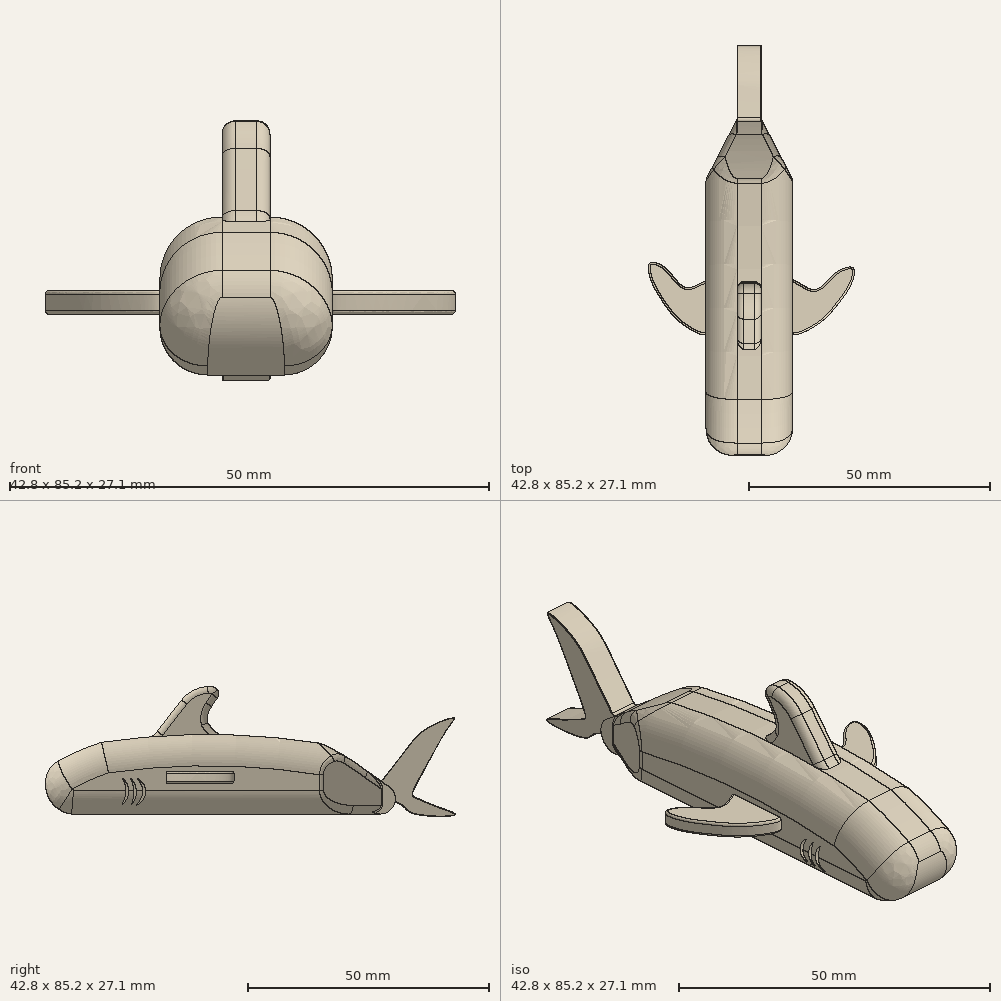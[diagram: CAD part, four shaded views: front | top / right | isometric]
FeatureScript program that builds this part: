
annotation { "Feature Type Name" : "Feature", "Feature Type Description" : "" }
export const myFeature = defineFeature(function(context is Context, id is Id, definition is map)
    precondition{}
    {
        {
            var Q0;
            Q0=qCreatedBy(makeId("Right.planeOp"),FACE);
            cPlane(context, id + "F0", {"entities" : qUnion([Q0]), "cplaneType" : CPlaneType.OFFSET, "offset" : 6.5 * mm, "width" : 150 * mm, "height" : 150 * mm});
        }
        {
            var Q0;
            Q0=qCreatedBy(makeId("Top.planeOp"),FACE);
            cPlane(context, id + "F1", {"entities" : qUnion([Q0]), "cplaneType" : CPlaneType.OFFSET, "offset" : 4.2 * mm, "oppositeDirection" : true, "width" : 150 * mm, "height" : 150 * mm});
        }
        {
            var Q0;
            Q0=qCreatedBy(makeId("Right.planeOp"),FACE);
            cPlane(context, id + "F2", {"entities" : qUnion([Q0]), "cplaneType" : CPlaneType.OFFSET, "offset" : 18 * mm, "width" : 150 * mm, "height" : 150 * mm});
        }
        {
            var Q0;
            Q0=qCreatedBy(makeId("Right.planeOp"),FACE);
            var sketch = newSketch(context, id + "F3", { "sketchPlane" : qUnion([Q0])});
            skLineSegment(sketch, "E0", {"start": v(-39.86, -13.02) * mm, "end": v(24.33, -13.02) * mm});
            skArc(sketch, "E1", {"start": v(-43.75, -2.7) * mm, "mid": v(-44.9, -9.03) * mm, "end": v(-39.86, -13.02) * mm});
            skArc(sketch, "E2", {"start": v(-33.67, 1.88) * mm, "mid": v(-38.84, -0.12) * mm, "end": v(-43.75, -2.7) * mm});
            skArc(sketch, "E3", {"start": v(11.79, 1.7) * mm, "mid": v(-10.93, 3.51) * mm, "end": v(-33.67, 1.88) * mm});
            skArc(sketch, "E4", {"start": v(21.4, -4.04) * mm, "mid": v(16.77, -0.87) * mm, "end": v(11.79, 1.7) * mm});
            skArc(sketch, "E5", {"start": v(25.54, -7) * mm, "mid": v(23.5, -5.48) * mm, "end": v(21.4, -4.04) * mm});
            skArc(sketch, "E6", {"start": v(24.33, -13.02) * mm, "mid": v(27.4, -10.51) * mm, "end": v(25.54, -7) * mm});
            skSolve(sketch);
        }
        {
            var Q0;
            {var subQ0=sQuery(id+"F3.wireOp",EDGE,"4997cbf1-64fe-4e0f-b577-89496dce1422");var subQ1=sQuery(id+"F3.wireOp",EDGE,"E0");var subQ2=makeQuery(id+"F3.imprint","INTERSECT",VERTEX,{"derivedFrom":[subQ1,subQ0]});Q0=makeQuery(id+"F3.imprint","IMPRINT",FACE,{"disambiguationData":[TD([[makeQuery(id+"F3.imprint","IMPRINT",EDGE,{"disambiguationData":[TD([[subQ2,-1.0]])],"derivedFrom":subQ1}),1.0]])]});}
            extrude(context, id + "F4", {"entities" : qUnion([Q0]), "depth" : 18 * mm, "offsetDistance" : 25 * mm});
        }
        {
            var Q0;
            Q0=makeQuery(id+"F4.opExtrude","CAP_EDGE",EDGE,{"disambiguationData":[OSD([sQuery(id+"F3.wireOp",EDGE,"E3")])],"isStart":false});
            var Q1;
            Q1=makeQuery(id+"F4.opExtrude","CAP_EDGE",EDGE,{"disambiguationData":[OSD([sQuery(id+"F3.wireOp",EDGE,"E3")])],"isStart":true});
            var Q2;
            Q2=makeQuery(id+"F4.opExtrude","CAP_EDGE",EDGE,{"disambiguationData":[OSD([sQuery(id+"F3.wireOp",EDGE,"E2")])],"isStart":true});
            var Q3;
            Q3=makeQuery(id+"F4.opExtrude","CAP_EDGE",EDGE,{"disambiguationData":[OSD([sQuery(id+"F3.wireOp",EDGE,"E2")])],"isStart":false});
            fillet(context, id + "F5", {"entities" : qUnion([Q0, Q1, Q2, Q3]), "radius" : 6.5 * mm, "allowEdgeOverflow" : false});
        }
        {
            var Q0;
            Q0=qCreatedBy(id+"F0.planeOp",FACE);
            var sketch = newSketch(context, id + "F6", { "sketchPlane" : qUnion([Q0])});
            skArc(sketch, "E7", {"start": v(-24.68, 2.43) * mm, "mid": v(-23.19, 3.05) * mm, "end": v(-22.01, 4.15) * mm});
            skArc(sketch, "E8", {"start": v(-16.96, 10.65) * mm, "mid": v(-19.5, 7.41) * mm, "end": v(-22.01, 4.15) * mm});
            skArc(sketch, "E9", {"start": v(-11.69, 13.48) * mm, "mid": v(-14.61, 12.6) * mm, "end": v(-16.96, 10.65) * mm});
            skArc(sketch, "E10", {"start": v(-9.52, 12.75) * mm, "mid": v(-10.5, 13.41) * mm, "end": v(-11.69, 13.48) * mm});
            skArc(sketch, "E11", {"start": v(-9.52, 11.03) * mm, "mid": v(-9.25, 11.89) * mm, "end": v(-9.52, 12.75) * mm});
            skArc(sketch, "E12", {"start": v(-9.52, 11.03) * mm, "mid": v(-10.16, 10.16) * mm, "end": v(-10.73, 9.25) * mm});
            skArc(sketch, "E13", {"start": v(-10.73, 9.25) * mm, "mid": v(-11.52, 7.68) * mm, "end": v(-11.54, 5.92) * mm});
            skArc(sketch, "E14", {"start": v(-11.54, 5.92) * mm, "mid": v(-9.81, 3.95) * mm, "end": v(-7.55, 2.65) * mm});
            skArc(sketch, "E15", {"start": v(-24.68, 2.43) * mm, "mid": v(-16.1, 1.6) * mm, "end": v(-7.55, 2.65) * mm});
            skSolve(sketch);
        }
        {
            var Q0;
            Q0 = qSketchRegion(id + "F6", true);
            extrude(context, id + "F7", {"entities" : qUnion([Q0]), "depth" : 5 * mm, "offsetDistance" : 25 * mm});
        }
        {
            var Q0;
            Q0=makeQuery(id+"F7.opExtrude","CAP_EDGE",EDGE,{"disambiguationData":[OSD([sQuery(id+"F6.wireOp",EDGE,"E11")])],"isStart":false});
            var Q1;
            Q1=makeQuery(id+"F7.opExtrude","CAP_EDGE",EDGE,{"disambiguationData":[OSD([sQuery(id+"F6.wireOp",EDGE,"E12")])],"isStart":false});
            var Q2;
            Q2=makeQuery(id+"F7.opExtrude","CAP_EDGE",EDGE,{"disambiguationData":[OSD([sQuery(id+"F6.wireOp",EDGE,"E13")])],"isStart":false});
            var Q3;
            Q3=makeQuery(id+"F7.opExtrude","CAP_EDGE",EDGE,{"disambiguationData":[OSD([sQuery(id+"F6.wireOp",EDGE,"E14")])],"isStart":false});
            var Q4;
            Q4=makeQuery(id+"F7.opExtrude","CAP_EDGE",EDGE,{"disambiguationData":[OSD([sQuery(id+"F6.wireOp",EDGE,"E10")])],"isStart":false});
            var Q5;
            Q5=makeQuery(id+"F7.opExtrude","CAP_EDGE",EDGE,{"disambiguationData":[OSD([sQuery(id+"F6.wireOp",EDGE,"E10")])],"isStart":true});
            var Q6;
            Q6=makeQuery(id+"F7.opExtrude","CAP_EDGE",EDGE,{"disambiguationData":[OSD([sQuery(id+"F6.wireOp",EDGE,"E11")])],"isStart":true});
            var Q7;
            Q7=makeQuery(id+"F7.opExtrude","CAP_EDGE",EDGE,{"disambiguationData":[OSD([sQuery(id+"F6.wireOp",EDGE,"E12")])],"isStart":true});
            var Q8;
            Q8=makeQuery(id+"F7.opExtrude","CAP_EDGE",EDGE,{"disambiguationData":[OSD([sQuery(id+"F6.wireOp",EDGE,"E13")])],"isStart":true});
            var Q9;
            Q9=makeQuery(id+"F7.opExtrude","CAP_EDGE",EDGE,{"disambiguationData":[OSD([sQuery(id+"F6.wireOp",EDGE,"E14")])],"isStart":true});
            var Q10;
            Q10=makeQuery(id+"F7.opExtrude","CAP_EDGE",EDGE,{"disambiguationData":[OSD([sQuery(id+"F6.wireOp",EDGE,"E9")])],"isStart":false});
            var Q11;
            Q11=makeQuery(id+"F7.opExtrude","CAP_EDGE",EDGE,{"disambiguationData":[OSD([sQuery(id+"F6.wireOp",EDGE,"E8")])],"isStart":false});
            var Q12;
            Q12=makeQuery(id+"F7.opExtrude","CAP_EDGE",EDGE,{"disambiguationData":[OSD([sQuery(id+"F6.wireOp",EDGE,"E7")])],"isStart":false});
            var Q13;
            Q13=makeQuery(id+"F7.opExtrude","CAP_EDGE",EDGE,{"disambiguationData":[OSD([sQuery(id+"F6.wireOp",EDGE,"E7")])],"isStart":true});
            var Q14;
            Q14=makeQuery(id+"F7.opExtrude","CAP_EDGE",EDGE,{"disambiguationData":[OSD([sQuery(id+"F6.wireOp",EDGE,"E8")])],"isStart":true});
            var Q15;
            Q15=makeQuery(id+"F7.opExtrude","CAP_EDGE",EDGE,{"disambiguationData":[OSD([sQuery(id+"F6.wireOp",EDGE,"E9")])],"isStart":true});
            fillet(context, id + "F8", {"entities" : qUnion([Q0, Q1, Q2, Q3, Q4, Q5, Q6, Q7, Q8, Q9, Q10, Q11, Q12, Q13, Q14, Q15]), "radius" : 1.4 * mm, "tangentPropagation" : true, "allowEdgeOverflow" : false});
        }
        {
            var Q0;
            Q0=makeQuery(id+"F5.opFillet","BLEND_EDGE",EDGE,{"blendedFrom":[makeQuery(id+"F4.opExtrude","CAP_EDGE",EDGE,{"disambiguationData":[OSD([sQuery(id+"F3.wireOp",EDGE,"E3")])],"isStart":true}),makeQuery(id+"F4.opExtrude","SWEPT_FACE",FACE,{"disambiguationData":[OSD([sQuery(id+"F3.wireOp",EDGE,"E5")])]})],"blendedInto":[makeQuery(id+"F4.opExtrude","SWEPT_FACE",FACE,{"disambiguationData":[OSD([sQuery(id+"F3.wireOp",EDGE,"E5")])]})]});
            var Q1;
            Q1=makeQuery(id+"F5.opFillet","BLEND_EDGE",EDGE,{"blendedFrom":[makeQuery(id+"F4.opExtrude","CAP_EDGE",EDGE,{"disambiguationData":[OSD([sQuery(id+"F3.wireOp",EDGE,"E3")])],"isStart":true}),makeQuery(id+"F4.opExtrude","SWEPT_FACE",FACE,{"disambiguationData":[OSD([sQuery(id+"F3.wireOp",EDGE,"E4")])]})],"blendedInto":[makeQuery(id+"F4.opExtrude","SWEPT_FACE",FACE,{"disambiguationData":[OSD([sQuery(id+"F3.wireOp",EDGE,"E4")])]})]});
            var Q2;
            Q2=makeQuery(id+"F5.opFillet","BLEND_EDGE",EDGE,{"blendedFrom":[makeQuery(id+"F4.opExtrude","CAP_EDGE",EDGE,{"disambiguationData":[OSD([sQuery(id+"F3.wireOp",EDGE,"E3")])],"isStart":false}),makeQuery(id+"F4.opExtrude","SWEPT_FACE",FACE,{"disambiguationData":[OSD([sQuery(id+"F3.wireOp",EDGE,"E4")])]})],"blendedInto":[makeQuery(id+"F4.opExtrude","SWEPT_FACE",FACE,{"disambiguationData":[OSD([sQuery(id+"F3.wireOp",EDGE,"E4")])]})]});
            var Q3;
            Q3=makeQuery(id+"F5.opFillet","BLEND_EDGE",EDGE,{"blendedFrom":[makeQuery(id+"F4.opExtrude","CAP_EDGE",EDGE,{"disambiguationData":[OSD([sQuery(id+"F3.wireOp",EDGE,"E3")])],"isStart":false}),makeQuery(id+"F4.opExtrude","SWEPT_FACE",FACE,{"disambiguationData":[OSD([sQuery(id+"F3.wireOp",EDGE,"E5")])]})],"blendedInto":[makeQuery(id+"F4.opExtrude","SWEPT_FACE",FACE,{"disambiguationData":[OSD([sQuery(id+"F3.wireOp",EDGE,"E5")])]})]});
            fillet(context, id + "F9", {"entities" : qUnion([Q0, Q1, Q2, Q3]), "radius" : 3.6 * mm, "tangentPropagation" : true, "allowEdgeOverflow" : false});
        }
        {
            var Q0;
            Q0=makeQuery(id+"F5.opFillet","BLEND_EDGE",EDGE,{"blendedFrom":[makeQuery(id+"F4.opExtrude","CAP_EDGE",EDGE,{"disambiguationData":[OSD([sQuery(id+"F3.wireOp",EDGE,"E3")])],"isStart":true}),makeQuery(id+"F4.opExtrude","SWEPT_FACE",FACE,{"disambiguationData":[OSD([sQuery(id+"F3.wireOp",EDGE,"E6")])]})],"blendedInto":[makeQuery(id+"F4.opExtrude","SWEPT_FACE",FACE,{"disambiguationData":[OSD([sQuery(id+"F3.wireOp",EDGE,"E6")])]})]});
            var Q1;
            Q1=makeQuery(id+"F5.opFillet","BLEND_EDGE",EDGE,{"blendedFrom":[makeQuery(id+"F4.opExtrude","CAP_EDGE",EDGE,{"disambiguationData":[OSD([sQuery(id+"F3.wireOp",EDGE,"E3")])],"isStart":false}),makeQuery(id+"F4.opExtrude","SWEPT_FACE",FACE,{"disambiguationData":[OSD([sQuery(id+"F3.wireOp",EDGE,"E6")])]})],"blendedInto":[makeQuery(id+"F4.opExtrude","SWEPT_FACE",FACE,{"disambiguationData":[OSD([sQuery(id+"F3.wireOp",EDGE,"E6")])]})]});
            var Q2;
            Q2=makeQuery(id+"F4.opExtrude","CAP_EDGE",EDGE,{"disambiguationData":[OSD([sQuery(id+"F3.wireOp",EDGE,"E6")])],"isStart":false});
            var Q3;
            Q3=makeQuery(id+"F4.opExtrude","CAP_EDGE",EDGE,{"disambiguationData":[OSD([sQuery(id+"F3.wireOp",EDGE,"E6")])],"isStart":true});
            fillet(context, id + "F10", {"entities" : qUnion([Q0, Q1, Q2, Q3]), "radius" : 5 * mm, "tangentPropagation" : true, "allowEdgeOverflow" : false});
        }
        {
            var Q0;
            Q0=qCreatedBy(id+"F1.planeOp",FACE);
            var sketch = newSketch(context, id + "F11", { "sketchPlane" : qUnion([Q0])});
            skFitSpline(sketch, "E16", {"points": [v(0.02, -20.11) * mm, v(-5.11, -17.8) * mm, v(-9.1, -13.16) * mm, v(-11.62, -8.34) * mm, v(-11.54, -5.22) * mm, v(-8.96, -5.93) * mm, v(-6.63, -8.29) * mm, v(-3.49, -10.42) * mm, v(1, -8.86) * mm, v(0.41, -15.55) * mm, v(0.02, -20.11) * mm]});
            skFitSpline(sketch, "E17.MirrorC", {"points": [v(17.75, -20.11) * mm, v(23.05, -18.26) * mm, v(27.44, -13.98) * mm, v(30.36, -9.4) * mm, v(30.56, -6.28) * mm, v(27.93, -6.77) * mm, v(25.4, -8.91) * mm, v(22.08, -10.76) * mm, v(17.75, -8.82) * mm, v(17.75, -15.54) * mm, v(17.75, -20.11) * mm]});
            skSolve(sketch);
        }
        {
            var Q0;
            Q0=makeQuery(id+"F11.imprint","IMPRINT",FACE,{"disambiguationData":[TD([[makeQuery(id+"F11.imprint","IMPRINT",EDGE,{"derivedFrom":sQuery(id+"F11.wireOp",EDGE,"E17.MirrorC")}),1.0]])]});
            var Q1;
            Q1=makeQuery(id+"F11.imprint","IMPRINT",FACE,{"disambiguationData":[TD([[makeQuery(id+"F11.imprint","IMPRINT",EDGE,{"derivedFrom":sQuery(id+"F11.wireOp",EDGE,"E16")}),-1.0]])]});
            extrude(context, id + "F12", {"entities" : qUnion([Q0, Q1]), "operationType" : NewBodyOperationType.ADD, "oppositeDirection" : true, "depth" : 2.5 * mm, "offsetDistance" : 25 * mm});
        }
        {
            var Q0;
            Q0=makeQuery(id+"F12.opExtrude","CAP_EDGE",EDGE,{"disambiguationData":[OSD([sQuery(id+"F11.wireOp",EDGE,"E16")])],"isStart":true});
            var Q1;
            Q1=makeQuery(id+"F12.opExtrude","CAP_EDGE",EDGE,{"disambiguationData":[OSD([sQuery(id+"F11.wireOp",EDGE,"E16")])],"isStart":false});
            var Q2;
            Q2=makeQuery(id+"F12.opExtrude","CAP_EDGE",EDGE,{"disambiguationData":[OSD([sQuery(id+"F11.wireOp",EDGE,"E17.MirrorC")])],"isStart":true});
            var Q3;
            Q3=makeQuery(id+"F12.opExtrude","CAP_EDGE",EDGE,{"disambiguationData":[OSD([sQuery(id+"F11.wireOp",EDGE,"E17.MirrorC")])],"isStart":false});
            fillet(context, id + "F13", {"entities" : qUnion([Q0, Q1, Q2, Q3]), "radius" : 0.4 * mm, "tangentPropagation" : true, "allowEdgeOverflow" : false});
        }
        {
            var Q0;
            Q0=makeQuery(id+"F4.opExtrude","SWEPT_EDGE",EDGE,{"disambiguationData":[OSD([sQuery(id+"F3.wireOp",EDGE,"E1"),sQuery(id+"F3.wireOp",EDGE,"E2")])]});
            fillet(context, id + "F14", {"entities" : qUnion([Q0]), "radius" : 5 * mm, "tangentPropagation" : true, "allowEdgeOverflow" : false});
        }
        {
            var Q0;
            Q0=qCreatedBy(id+"F0.planeOp",FACE);
            var sketch = newSketch(context, id + "F15", { "sketchPlane" : qUnion([Q0])});
            skFitSpline(sketch, "E18", {"points": [v(24.52, -6.22) * mm, v(30.23, 1.12) * mm, v(33.9, 4.72) * mm, v(38.73, 6.85) * mm, v(39.75, 6.85) * mm, v(38.44, 4.82) * mm, v(33.5, -3.75) * mm, v(31.03, -9.12) * mm, v(31.61, -9.56) * mm, v(35.68, -11.3) * mm, v(39.9, -13.19) * mm, v(31.03, -12.9) * mm, v(28.7, -11.16) * mm, v(23.19, -8.54) * mm, v(24.52, -6.22) * mm]});
            skSolve(sketch);
        }
        {
            var Q0;
            Q0 = qSketchRegion(id + "F15", true);
            extrude(context, id + "F16", {"entities" : qUnion([Q0]), "operationType" : NewBodyOperationType.ADD, "depth" : 5 * mm, "offsetDistance" : 25 * mm});
        }
        {
            var Q0;
            Q0=qCreatedBy(id+"F2.planeOp",FACE);
            var sketch = newSketch(context, id + "F17", { "sketchPlane" : qUnion([Q0])});
            skArc(sketch, "E19", {"start": v(-26.47, -11.25) * mm, "mid": v(-25.12, -8.5) * mm, "end": v(-26.22, -5.65) * mm});
            skArc(sketch, "E20", {"start": v(-26.47, -11.25) * mm, "mid": v(-24.45, -8.54) * mm, "end": v(-26.22, -5.65) * mm});
            skArc(sketch, "E21", {"start": v(-27.46, -11.18) * mm, "mid": v(-26.4, -8.4) * mm, "end": v(-27.57, -5.65) * mm});
            skArc(sketch, "E22", {"start": v(-27.46, -11.18) * mm, "mid": v(-26.95, -8.4) * mm, "end": v(-27.57, -5.65) * mm});
            skArc(sketch, "E23", {"start": v(-29.43, -11.12) * mm, "mid": v(-28.6, -8.41) * mm, "end": v(-29.24, -5.65) * mm});
            skArc(sketch, "E24", {"start": v(-29.43, -11.12) * mm, "mid": v(-27.96, -8.43) * mm, "end": v(-29.24, -5.65) * mm});
            skSolve(sketch);
        }
        {
            var Q0;
            Q0 = qSketchRegion(id + "F17", true);
            extrude(context, id + "F18", {"entities" : qUnion([Q0]), "operationType" : NewBodyOperationType.REMOVE, "oppositeDirection" : true, "depth" : 1.3 * mm, "offsetDistance" : 25 * mm});
        }
        {
            var Q0;
            Q0=qCreatedBy(makeId("Right.planeOp"),FACE);
            var sketch = newSketch(context, id + "F19", { "sketchPlane" : qUnion([Q0])});
            skArc(sketch, "E25", {"start": v(-26.42, -11.26) * mm, "mid": v(-25.07, -8.52) * mm, "end": v(-26.16, -5.67) * mm});
            skArc(sketch, "E26", {"start": v(-26.42, -11.26) * mm, "mid": v(-24.4, -8.55) * mm, "end": v(-26.16, -5.67) * mm});
            skArc(sketch, "E27", {"start": v(-27.4, -11.2) * mm, "mid": v(-26.35, -8.4) * mm, "end": v(-27.51, -5.67) * mm});
            skArc(sketch, "E28", {"start": v(-27.4, -11.2) * mm, "mid": v(-26.9, -8.42) * mm, "end": v(-27.51, -5.67) * mm});
            skArc(sketch, "E29", {"start": v(-29.38, -11.13) * mm, "mid": v(-28.54, -8.42) * mm, "end": v(-29.18, -5.67) * mm});
            skArc(sketch, "E30", {"start": v(-29.38, -11.13) * mm, "mid": v(-27.9, -8.45) * mm, "end": v(-29.18, -5.67) * mm});
            skSolve(sketch);
        }
        {
            var Q0;
            Q0 = qSketchRegion(id + "F19", true);
            extrude(context, id + "F20", {"entities" : qUnion([Q0]), "operationType" : NewBodyOperationType.REMOVE, "depth" : 1.3 * mm, "offsetDistance" : 25 * mm});
        }
        {
            var Q0;
            Q0=makeQuery(id+"F16.opExtrude","CAP_EDGE",EDGE,{"disambiguationData":[OSD([sQuery(id+"F15.wireOp",EDGE,"E18")])],"isStart":true});
            var Q1;
            Q1=makeQuery(id+"F16.opExtrude","CAP_EDGE",EDGE,{"disambiguationData":[OSD([sQuery(id+"F15.wireOp",EDGE,"E18")])],"isStart":false});
            fillet(context, id + "F21", {"entities" : qUnion([Q0, Q1]), "radius" : 0.1 * mm, "tangentPropagation" : true, "allowEdgeOverflow" : false});
        }
        {
            var Q0;
            Q0=qCreatedBy(makeId("Top.planeOp"),FACE);
            var sketch = newSketch(context, id + "F22", { "sketchPlane" : qUnion([Q0])});
            skLineSegment(sketch, "E31", {"start": v(0, 12.03) * mm, "end": v(6.5, 24.63) * mm});
            skLineSegment(sketch, "E32", {"start": v(6.5, 24.63) * mm, "end": v(6.5, 32.2) * mm});
            skLineSegment(sketch, "E33", {"start": v(6.5, 32.2) * mm, "end": v(0, 37.24) * mm});
            skLineSegment(sketch, "E34", {"start": v(0, 37.24) * mm, "end": v(0, 12.03) * mm});
            skLineSegment(sketch, "E35.MirrorCS", {"start": v(18.03, 37.24) * mm, "end": v(18.07, 11.96) * mm});
            skLineSegment(sketch, "E36.MirrorCS", {"start": v(11.5, 32.2) * mm, "end": v(18.03, 37.24) * mm});
            skLineSegment(sketch, "E37.MirrorCS", {"start": v(18.07, 11.96) * mm, "end": v(11.5, 24.6) * mm});
            skLineSegment(sketch, "E38.MirrorCS", {"start": v(11.5, 24.6) * mm, "end": v(11.5, 32.2) * mm});
            skSolve(sketch);
        }
        {
            var Q0;
            Q0 = qSketchRegion(id + "F22", true);
            extrude(context, id + "F23", {"entities" : qUnion([Q0]), "operationType" : NewBodyOperationType.REMOVE, "oppositeDirection" : true, "depth" : 100 * mm, "offsetDistance" : 25 * mm});
        }
        {
            var Q0;
            Q0=makeQuery(id+"F23.boolean.opBoolean","INTERSECT",EDGE,{"derivedFrom":[makeQuery(id+"F4.opExtrude","SWEPT_FACE",FACE,{"disambiguationData":[OSD([sQuery(id+"F3.wireOp",EDGE,"E5")])]}),makeQuery(id+"F23.opExtrude","SWEPT_FACE",FACE,{"disambiguationData":[OSD([sQuery(id+"F22.wireOp",EDGE,"E37.MirrorCS")])]})]});
            var Q1;
            Q1=makeQuery(id+"F23.boolean.opBoolean","INTERSECT",EDGE,{"derivedFrom":[makeQuery(id+"F4.opExtrude","SWEPT_FACE",FACE,{"disambiguationData":[OSD([sQuery(id+"F3.wireOp",EDGE,"E4")])]}),makeQuery(id+"F23.opExtrude","SWEPT_FACE",FACE,{"disambiguationData":[OSD([sQuery(id+"F22.wireOp",EDGE,"E37.MirrorCS")])]})]});
            var Q2;
            Q2=makeQuery(id+"F23.boolean.opBoolean","INTERSECT",EDGE,{"derivedFrom":[makeQuery(id+"F4.opExtrude","SWEPT_FACE",FACE,{"disambiguationData":[OSD([sQuery(id+"F3.wireOp",EDGE,"E0")])]}),makeQuery(id+"F23.opExtrude","SWEPT_FACE",FACE,{"disambiguationData":[OSD([sQuery(id+"F22.wireOp",EDGE,"E37.MirrorCS")])]})]});
            var Q3;
            {var subQ0=sQuery(id+"F3.wireOp",EDGE,"E0");Q3=makeQuery(id+"F23.boolean.opBoolean","INTERSECT",EDGE,{"derivedFrom":[makeQuery(id+"F10.opFillet","BLEND_FACE",FACE,{"disambiguationData":[OSD([subQ0]),TDD([makeQuery(id+"F4.opExtrude","CAP_EDGE",EDGE,{"disambiguationData":[OSD([subQ0])],"isStart":false})])]}),makeQuery(id+"F23.opExtrude","SWEPT_FACE",FACE,{"disambiguationData":[OSD([sQuery(id+"F22.wireOp",EDGE,"E37.MirrorCS")])]})]});}
            var Q4;
            Q4=makeQuery(id+"F23.boolean.opBoolean","INTERSECT",EDGE,{"derivedFrom":[makeQuery(id+"F4.opExtrude","CAP_FACE",FACE,{"disambiguationData":[OSD([sQuery(id+"F3.wireOp",EDGE,"E0"),sQuery(id+"F3.wireOp",EDGE,"E1"),sQuery(id+"F3.wireOp",EDGE,"E2"),sQuery(id+"F3.wireOp",EDGE,"E3"),sQuery(id+"F3.wireOp",EDGE,"E4"),sQuery(id+"F3.wireOp",EDGE,"E5"),sQuery(id+"F3.wireOp",EDGE,"E6")])],"isStart":false}),makeQuery(id+"F23.opExtrude","SWEPT_FACE",FACE,{"disambiguationData":[OSD([sQuery(id+"F22.wireOp",EDGE,"E37.MirrorCS")])]})]});
            var Q5;
            {var subQ0=sQuery(id+"F3.wireOp",EDGE,"E4");var subQ1=sQuery(id+"F3.wireOp",EDGE,"E3");Q5=makeQuery(id+"F23.boolean.opBoolean","INTERSECT",EDGE,{"derivedFrom":[makeQuery(id+"F9.opFillet","BLEND_FACE",FACE,{"disambiguationData":[OSD([subQ1,subQ0]),TDD([makeQuery(id+"F5.opFillet","BLEND_EDGE",EDGE,{"blendedFrom":[makeQuery(id+"F4.opExtrude","CAP_EDGE",EDGE,{"disambiguationData":[OSD([subQ1])],"isStart":false}),makeQuery(id+"F4.opExtrude","SWEPT_FACE",FACE,{"disambiguationData":[OSD([subQ0])]})],"blendedInto":[makeQuery(id+"F4.opExtrude","SWEPT_FACE",FACE,{"disambiguationData":[OSD([subQ0])]})]})]),OD(1.0)]}),makeQuery(id+"F23.opExtrude","SWEPT_FACE",FACE,{"disambiguationData":[OSD([sQuery(id+"F22.wireOp",EDGE,"E37.MirrorCS")])]})]});}
            var Q6;
            Q6=makeQuery(id+"F23.boolean.opBoolean","INTERSECT",EDGE,{"derivedFrom":[makeQuery(id+"F4.opExtrude","SWEPT_FACE",FACE,{"disambiguationData":[OSD([sQuery(id+"F3.wireOp",EDGE,"E5")])]}),makeQuery(id+"F23.opExtrude","SWEPT_FACE",FACE,{"disambiguationData":[OSD([sQuery(id+"F22.wireOp",EDGE,"E31")])]})]});
            var Q7;
            {var subQ0=sQuery(id+"F3.wireOp",EDGE,"E0");Q7=makeQuery(id+"F23.boolean.opBoolean","INTERSECT",EDGE,{"derivedFrom":[makeQuery(id+"F10.opFillet","BLEND_FACE",FACE,{"disambiguationData":[OSD([subQ0]),TDD([makeQuery(id+"F4.opExtrude","CAP_EDGE",EDGE,{"disambiguationData":[OSD([subQ0])],"isStart":true})])]}),makeQuery(id+"F23.opExtrude","SWEPT_FACE",FACE,{"disambiguationData":[OSD([sQuery(id+"F22.wireOp",EDGE,"E31")])]})]});}
            var Q8;
            Q8=makeQuery(id+"F23.boolean.opBoolean","COPY",EDGE,{"derivedFrom":makeQuery(id+"F23.opExtrude","SWEPT_EDGE",EDGE,{"disambiguationData":[OSD([sQuery(id+"F22.wireOp",EDGE,"E31"),sQuery(id+"F22.wireOp",EDGE,"E34")])]})});
            var Q9;
            {var subQ0=sQuery(id+"F3.wireOp",EDGE,"E4");var subQ1=sQuery(id+"F3.wireOp",EDGE,"E3");Q9=makeQuery(id+"F23.boolean.opBoolean","INTERSECT",EDGE,{"derivedFrom":[makeQuery(id+"F9.opFillet","BLEND_FACE",FACE,{"disambiguationData":[OSD([subQ1,subQ0]),TDD([makeQuery(id+"F5.opFillet","BLEND_EDGE",EDGE,{"blendedFrom":[makeQuery(id+"F4.opExtrude","CAP_EDGE",EDGE,{"disambiguationData":[OSD([subQ1])],"isStart":true}),makeQuery(id+"F4.opExtrude","SWEPT_FACE",FACE,{"disambiguationData":[OSD([subQ0])]})],"blendedInto":[makeQuery(id+"F4.opExtrude","SWEPT_FACE",FACE,{"disambiguationData":[OSD([subQ0])]})]})]),OD(1.0)]}),makeQuery(id+"F23.opExtrude","SWEPT_FACE",FACE,{"disambiguationData":[OSD([sQuery(id+"F22.wireOp",EDGE,"E31")])]})]});}
            var Q10;
            {var subQ0=sQuery(id+"F3.wireOp",EDGE,"E3");Q10=makeQuery(id+"F23.boolean.opBoolean","INTERSECT",EDGE,{"derivedFrom":[makeQuery(id+"F9.opFillet","SPLIT",FACE,{"disambiguationData":[OD(1.0)],"derivedFrom":makeQuery(id+"F5.opFillet","BLEND_FACE",FACE,{"disambiguationData":[OSD([subQ0]),TDD([makeQuery(id+"F4.opExtrude","CAP_EDGE",EDGE,{"disambiguationData":[OSD([subQ0])],"isStart":true})])]})}),makeQuery(id+"F23.opExtrude","SWEPT_FACE",FACE,{"disambiguationData":[OSD([sQuery(id+"F22.wireOp",EDGE,"E31")])]})]});}
            fillet(context, id + "F24", {"entities" : qUnion([Q0, Q1, Q2, Q3, Q4, Q5, Q6, Q7, Q8, Q9, Q10]), "radius" : 1.8 * mm, "tangentPropagation" : true, "allowEdgeOverflow" : false});
        }
        {
            var Q0;
            Q0=makeQuery(id+"F23.boolean.opBoolean","COPY",EDGE,{"derivedFrom":makeQuery(id+"F23.opExtrude","SWEPT_EDGE",EDGE,{"disambiguationData":[OSD([sQuery(id+"F22.wireOp",EDGE,"E37.MirrorCS"),sQuery(id+"F22.wireOp",EDGE,"E38.MirrorCS")])]})});
            var Q1;
            Q1=makeQuery(id+"F16.boolean.opBoolean","INTERSECT",EDGE,{"derivedFrom":[makeQuery(id+"F4.opExtrude","SWEPT_FACE",FACE,{"disambiguationData":[OSD([sQuery(id+"F3.wireOp",EDGE,"E5")])]}),makeQuery(id+"F16.opExtrude","SWEPT_FACE",FACE,{"disambiguationData":[OSD([sQuery(id+"F15.wireOp",EDGE,"E18")])]})]});
            var Q2;
            Q2=makeQuery(id+"F23.boolean.opBoolean","COPY",EDGE,{"derivedFrom":makeQuery(id+"F23.opExtrude","SWEPT_EDGE",EDGE,{"disambiguationData":[OSD([sQuery(id+"F22.wireOp",EDGE,"E31"),sQuery(id+"F22.wireOp",EDGE,"E32")])]})});
            fillet(context, id + "F25", {"entities" : qUnion([Q0, Q1, Q2]), "radius" : 0.6 * mm, "tangentPropagation" : true, "allowEdgeOverflow" : false});
        }
    });
